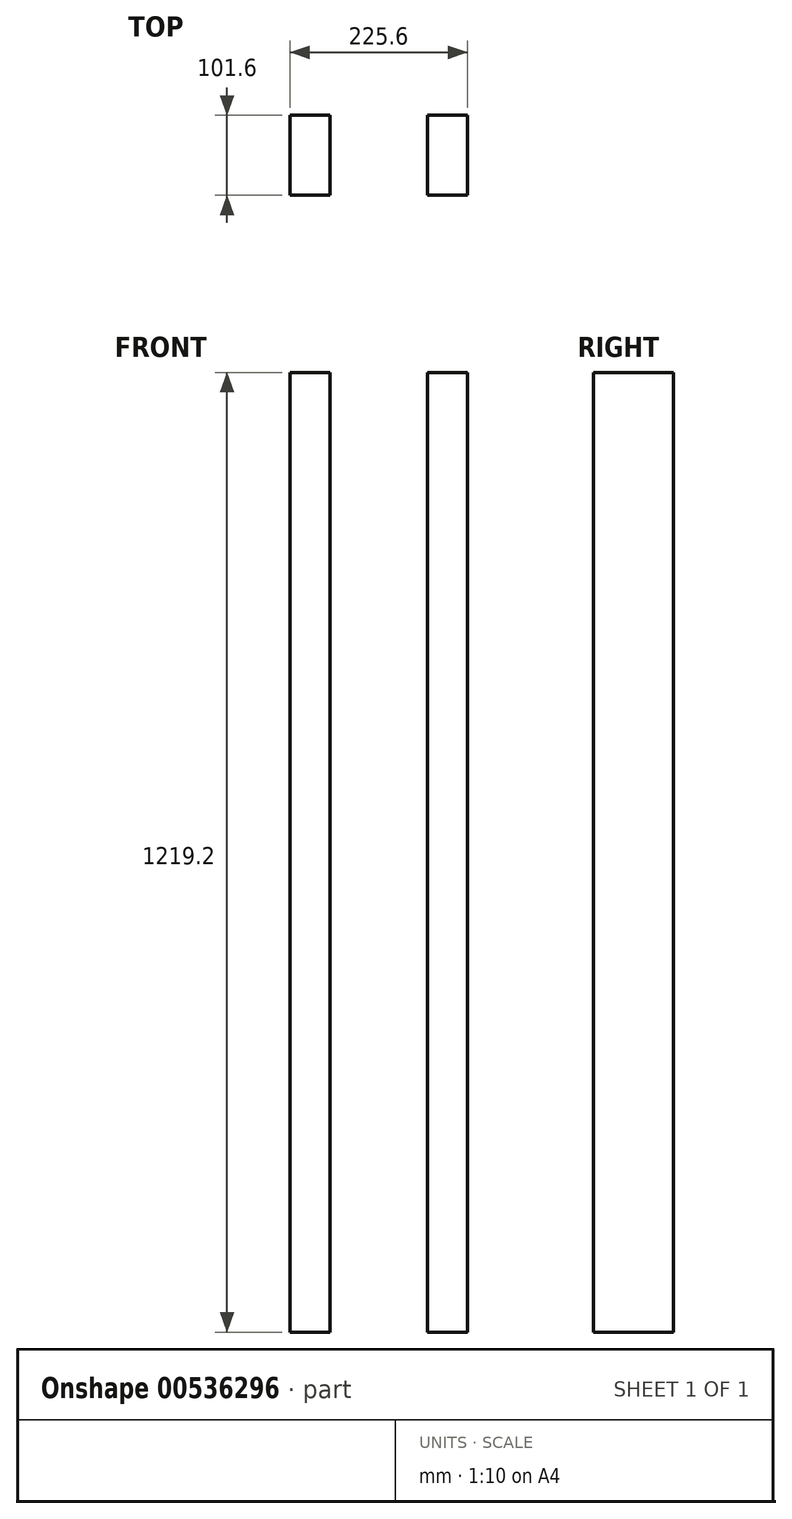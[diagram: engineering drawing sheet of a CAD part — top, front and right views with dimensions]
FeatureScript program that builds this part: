
annotation { "Feature Type Name" : "Feature", "Feature Type Description" : "" }
export const myFeature = defineFeature(function(context is Context, id is Id, definition is map)
    precondition{}
    {
        {
            var Q0;
            Q0=qCreatedBy(makeId("Front.planeOp"),FACE);
            var sketch = newSketch(context, id + "F0", { "sketchPlane" : qUnion([Q0])});
            skLineSegment(sketch, "E0.bottom", {"start": v(-74.82, 0) * mm, "end": v(-125.62, 0) * mm});
            skLineSegment(sketch, "E0.top", {"start": v(-74.82, 1219.2) * mm, "end": v(-125.62, 1219.2) * mm});
            skLineSegment(sketch, "E0.left", {"start": v(-74.82, 0) * mm, "end": v(-74.82, 1219.2) * mm});
            skLineSegment(sketch, "E0.right", {"start": v(-125.62, 0) * mm, "end": v(-125.62, 1219.2) * mm});
            skSolve(sketch);
        }
        {
            var Q0;
            Q0=qSketchRegion(id+"F0",true);
            extrude(context, id + "F1", {"entities" : qUnion([Q0]), "depth" : 101.6 * mm, "offsetDistance" : 25.4 * mm});
        }
        {
            var Q0;
            Q0=qCreatedBy(makeId("Front.planeOp"),FACE);
            var sketch = newSketch(context, id + "F2", { "sketchPlane" : qUnion([Q0])});
            skLineSegment(sketch, "E1.bottom", {"start": v(49.18, 0) * mm, "end": v(99.98, 0) * mm});
            skLineSegment(sketch, "E1.top", {"start": v(49.18, 1219.2) * mm, "end": v(99.98, 1219.2) * mm});
            skLineSegment(sketch, "E1.left", {"start": v(49.18, 0) * mm, "end": v(49.18, 1219.2) * mm});
            skLineSegment(sketch, "E1.right", {"start": v(99.98, 0) * mm, "end": v(99.98, 1219.2) * mm});
            skSolve(sketch);
        }
        {
            var Q0;
            Q0=qSketchRegion(id+"F2",true);
            extrude(context, id + "F3", {"entities" : qUnion([Q0]), "depth" : 101.6 * mm, "offsetDistance" : 25.4 * mm});
        }
    });
